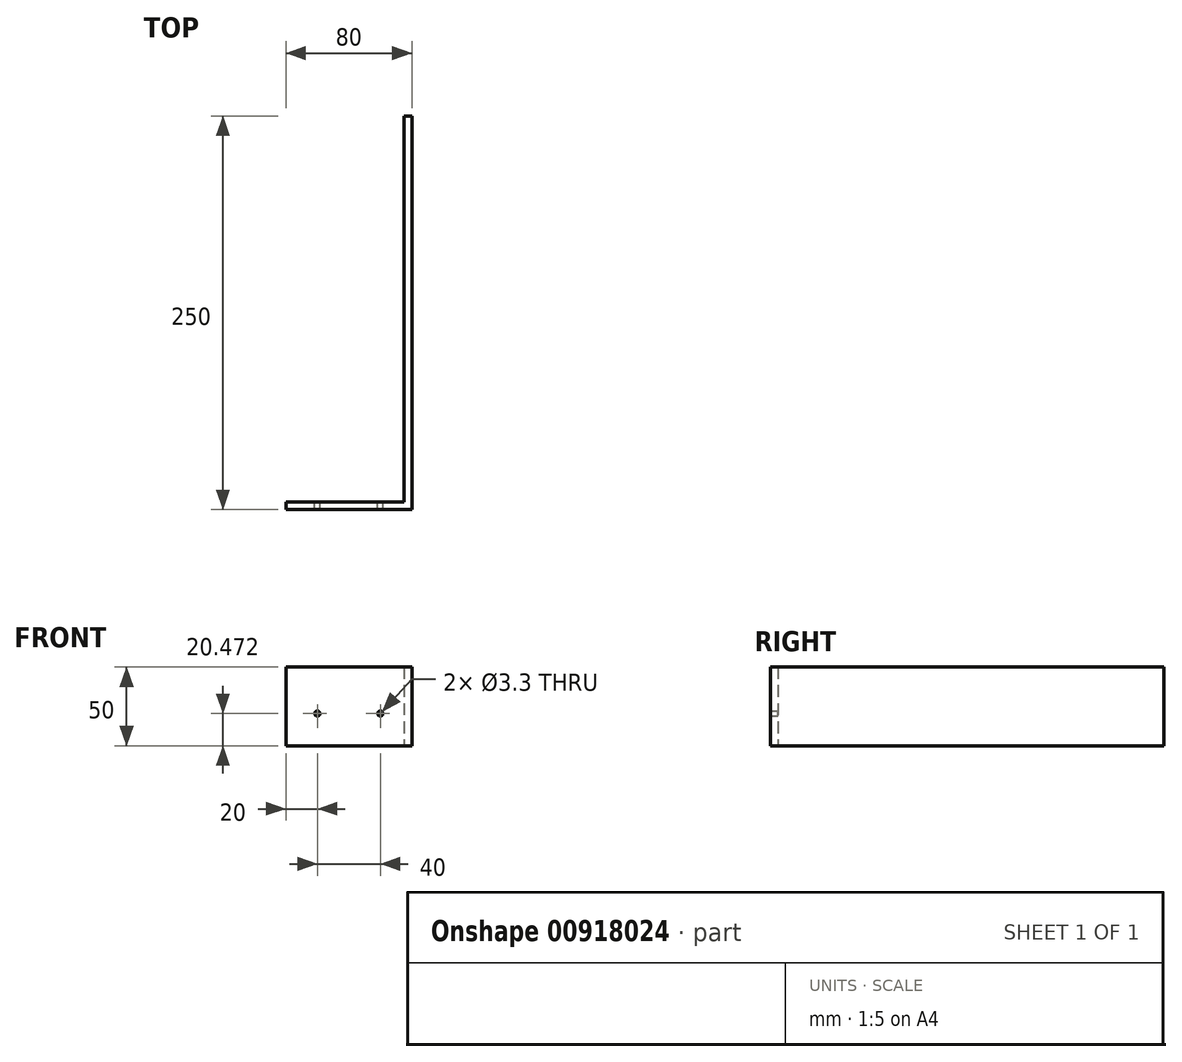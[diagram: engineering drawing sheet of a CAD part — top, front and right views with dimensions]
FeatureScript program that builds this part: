
annotation { "Feature Type Name" : "Feature", "Feature Type Description" : "" }
export const myFeature = defineFeature(function(context is Context, id is Id, definition is map)
    precondition{}
    {
        {
            var Q0;
            Q0=qCreatedBy(makeId("Front.planeOp"),FACE);
            var sketch = newSketch(context, id + "F0", { "sketchPlane" : qUnion([Q0])});
            skLineSegment(sketch, "E0.top", {"start": v(0, -100) * mm, "end": v(80, -100) * mm});
            skLineSegment(sketch, "E1", {"start": v(20, -79.53) * mm, "end": v(60, -79.53) * mm, "construction": true});
            skCircle(sketch, "E2", {"center": v(60, -79.53) * mm, "radius": 1.65 * mm});
            skCircle(sketch, "E3", {"center": v(20, -79.53) * mm, "radius": 1.65 * mm});
            skLineSegment(sketch, "E4", {"start": v(0, -50) * mm, "end": v(80, -50) * mm});
            skLineSegment(sketch, "E5", {"start": v(0, -50) * mm, "end": v(0, -100) * mm});
            skLineSegment(sketch, "E6", {"start": v(80, -50) * mm, "end": v(80, -100) * mm});
            skSolve(sketch);
        }
        {
            var Q0;
            Q0=qSketchRegion(id+"F0",true);
            extrude(context, id + "F1", {"entities" : qUnion([Q0]), "depth" : 5 * mm, "offsetDistance" : 25 * mm});
        }
        {
            var Q0;
            Q0=makeQuery(id+"F1.opExtrude","SWEPT_FACE",FACE,{"disambiguationData":[OSD([sQuery(id+"F0.wireOp",EDGE,"E6")])]});
            var sketch = newSketch(context, id + "F2", { "sketchPlane" : qUnion([Q0])});
            skLineSegment(sketch, "E7", {"start": v(-5, -50) * mm, "end": v(245, -50) * mm});
            skLineSegment(sketch, "E8", {"start": v(-5, -100) * mm, "end": v(245, -100) * mm});
            skLineSegment(sketch, "E9", {"start": v(245, -50) * mm, "end": v(245, -100) * mm});
            skSolve(sketch);
        }
        {
            var Q0;
            {var subQ2=sQuery(id+"F2.wireOp",EDGE,"E9");Q0=makeQuery(id+"F2.imprint","IMPRINT",FACE,{"disambiguationData":[TD([[makeQuery(id+"F2.imprint","IMPRINT",EDGE,{"derivedFrom":subQ2}),-1.0]])]});}
            extrude(context, id + "F3", {"entities" : qUnion([Q0]), "operationType" : NewBodyOperationType.ADD, "oppositeDirection" : true, "depth" : 5 * mm, "offsetDistance" : 25 * mm});
        }
    });
